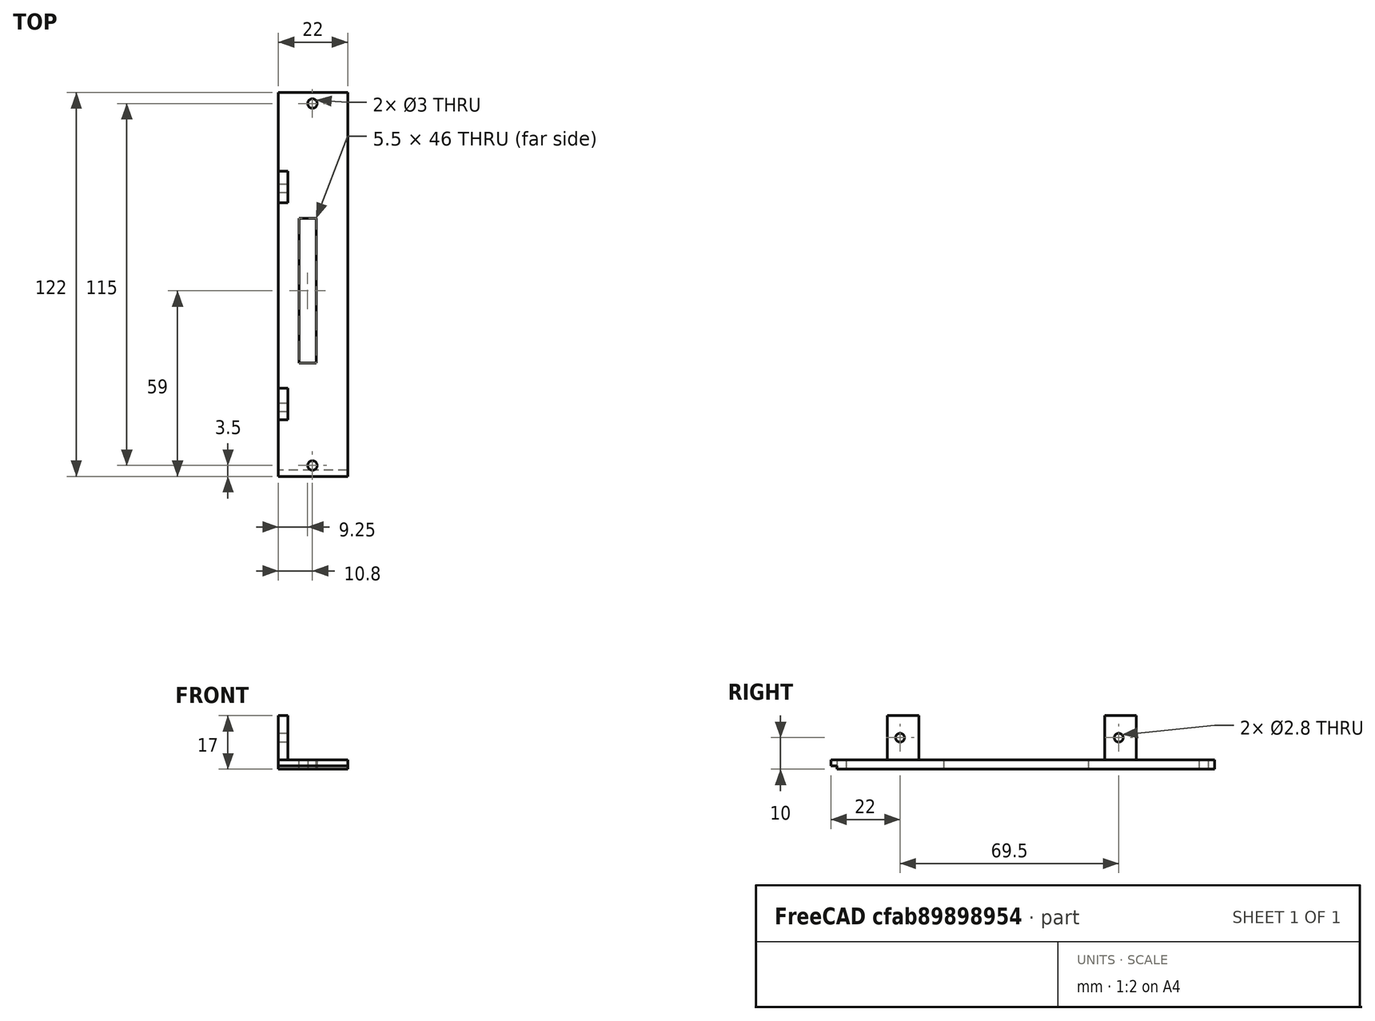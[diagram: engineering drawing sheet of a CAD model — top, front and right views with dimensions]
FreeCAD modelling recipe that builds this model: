
FCSTD DOCUMENT  (FreeCAD 0.20R29177 +426 (Git))
Label: N2630-A2000-Bracket
Comment: Amiga 2000 support brack for the N2630.
License: All rights reserved
objects: PartDesign::SubtractiveCylinder×4, PartDesign::AdditiveBox×3, PartDesign::SubtractiveBox×2, PartDesign::Body×1
note: 19 computed .brp shape members not serialized (recipe doc carries the construction recipe); baked Part::Feature solids carry a one-line shape summary decoded from their .brp

FEATURE [PartDesign::AdditiveBox] Box
  AttacherType = Attacher::AttachEngine3D
  AttachmentOffset = pos=(-10,-62.5,0) rot=(0,0,1;0rad)
  Height = 3
  Length = 22
  MapMode = 5
  Placement = pos=(-10,-62.5,0) rot=(0,0,1;0rad)
  Refine = true
  Support = -> [XY_Plane]
  Width = 122
FEATURE [PartDesign::AdditiveBox] Box001  label="Lower Brace"
  AttacherType = Attacher::AttachEngine3D
  AttachmentOffset = pos=(-44.5,0,-10) rot=(0,0,1;0rad)
  BaseFeature = -> Box
  Height = 3
  Length = 10
  MapMode = 2
  Placement = pos=(-10,-44.5,7.7e-15) rot=(0.57735,0.57735,0.57735;2.0944rad)
  Refine = true
  Support = -> [YZ_Plane]
  Width = 17
FEATURE [PartDesign::AdditiveBox] Box002  label="Upper Brace"
  AttacherType = Attacher::AttachEngine3D
  AttachmentOffset = pos=(24.5,0,-10) rot=(0,0,1;0rad)
  BaseFeature = -> Box001
  Height = 3
  Length = 10
  MapMode = 2
  Placement = pos=(-10,24.5,-7.7e-15) rot=(0.57735,0.57735,0.57735;2.0944rad)
  Refine = true
  Support = -> [YZ_Plane]
  Width = 17
FEATURE [PartDesign::SubtractiveBox] Box003  label="CFSlot"
  AttacherType = Attacher::AttachEngine3D
  AttachmentOffset = pos=(5,6.5,-4) rot=(0,0,1;0rad)
  BaseFeature = -> Box002
  Height = 5
  Length = 46
  MapMode = 5
  Placement = pos=(-3.5,19.5,-1) rot=(0,0,-1;1.5708rad)
  Support = -> [Box002]
  Width = 5.5
FEATURE [PartDesign::SubtractiveCylinder] Cylinder002  label="UpperMountingHole"
  Angle = 360
  AttacherType = Attacher::AttachEngine3D
  AttachmentOffset = pos=(-90.5,-6.8,-4) rot=(0,0,1;0rad)
  BaseFeature = -> Box003
  FirstAngle = 0
  Height = 5
  MapMode = 5
  Placement = pos=(0.8,-59,-1) rot=(0,0,1;1.5708rad)
  Radius = 1.5
  SecondAngle = 0
FEATURE [PartDesign::SubtractiveCylinder] Cylinder003  label="LowerMountingHole"
  Angle = 360
  AttacherType = Attacher::AttachEngine3D
  AttachmentOffset = pos=(115,0,-4) rot=(0,0,1;0rad)
  BaseFeature = -> Cylinder002
  FirstAngle = 0
  Height = 5
  MapMode = 5
  Placement = pos=(0.8,56,-1) rot=(0,0,1;1.5708rad)
  Radius = 1.5
  SecondAngle = 0
  Support = -> [Cylinder002]
FEATURE [PartDesign::SubtractiveBox] Box004  label="ShieldCutout"
  AttacherType = Attacher::AttachEngine3D
  AttachmentOffset = pos=(-118.5,-16,-4) rot=(0,0,1;0rad)
  BaseFeature = -> Cylinder003
  Height = 2
  Length = 2
  MapMode = 5
  Placement = pos=(16.8,-62.5,-1) rot=(0,0,1;1.5708rad)
  Support = -> [Cylinder003]
  Width = 30
FEATURE [PartDesign::SubtractiveCylinder] Cylinder  label="LowerBraceHole"
  Angle = 360
  AttacherType = Attacher::AttachEngine3D
  AttachmentOffset = pos=(-22,11,-4) rot=(0,0,1;0rad)
  BaseFeature = -> Box004
  FirstAngle = 0
  Height = 5
  MapMode = 5
  Placement = pos=(-6,-40.5,10) rot=(0.57735,-0.57735,-0.57735;2.0944rad)
  Radius = 1.4
  SecondAngle = 0
  Support = -> [Box004]
FEATURE [PartDesign::SubtractiveCylinder] Cylinder004  label="UpperBraceHole"
  Angle = 360
  AttacherType = Attacher::AttachEngine3D
  AttachmentOffset = pos=(-69.5,0,-4) rot=(0,0,1;0rad)
  BaseFeature = -> Cylinder
  FirstAngle = 0
  Height = 5
  MapMode = 5
  Placement = pos=(-6,29,10) rot=(0.57735,-0.57735,-0.57735;2.0944rad)
  Radius = 1.4
  SecondAngle = 0
  Support = -> [Cylinder]
FEATURE [PartDesign::Body] Body
  Group = -> [Box,Box001,Box002,Box003,Cylinder002,Cylinder003,Box004,Cylinder,Cylinder004]
  Origin = -> Origin
  Tip = -> Cylinder004
